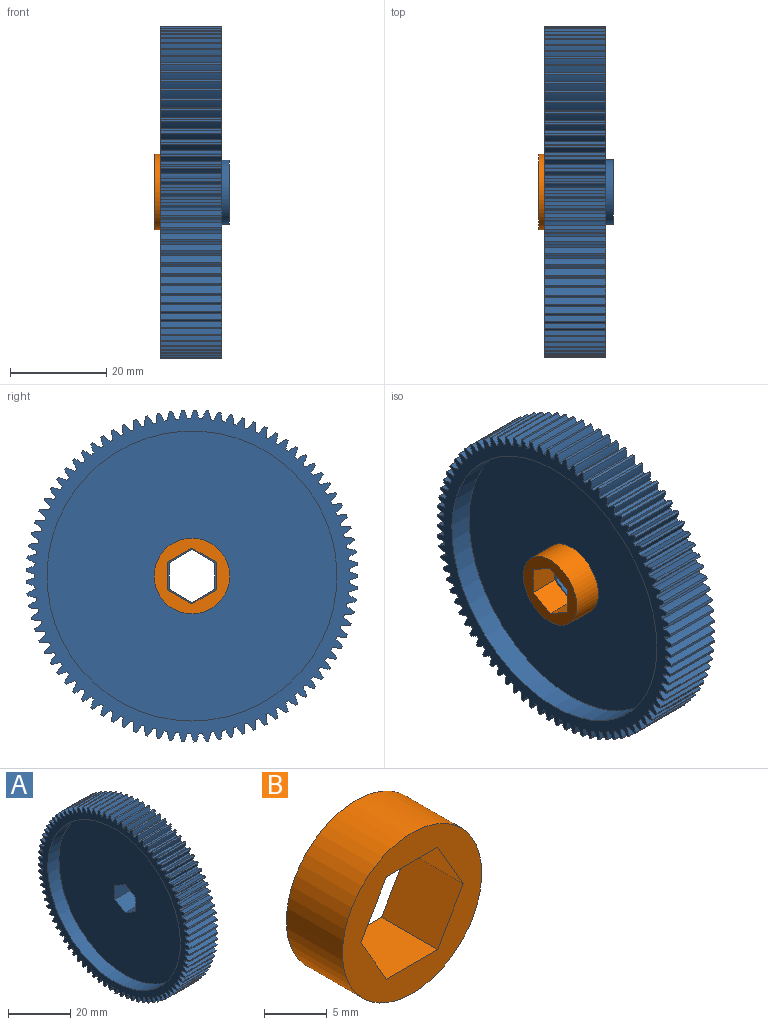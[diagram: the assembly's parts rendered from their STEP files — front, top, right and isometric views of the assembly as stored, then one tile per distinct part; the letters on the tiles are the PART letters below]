
ASSEMBLY  parts=2 mates=1
PART A: 354 faces, bbox 14.3x69x69.1 mm
  f0: cylinder r=30.16mm len=60.33mm, axis (-1,0,0), area 962.7mm2, adj f7,f353
  f1: cylinder r=30.16mm len=60.33mm, axis (1,0,0), area 962.7mm2, adj f8,f352
  f2: cylinder r=6.67mm len=13.34mm, axis (-1,0,0), area 279.3mm2, adj f345,f352
  f3: cylinder r=13.49mm len=12.7mm, axis (-1,0,0), area 24.3mm2, adj f7,f8,f185,f186
  f4: cylinder r=13.49mm len=12.7mm, axis (-1,0,0), area 24.3mm2, adj f7,f8,f187,f188
  f5: cylinder r=13.49mm len=12.7mm, axis (-1,0,0), area 24.3mm2, adj f7,f8,f252,f254
  f6: cylinder r=13.49mm len=12.7mm, axis (-1,0,0), area 24.3mm2, adj f7,f8,f253,f256
  f7: plane 69.05x69.04mm, normal (-1,0,0), area 690.3mm2, adj f0,f3,f4,f5,f6,f9,f10,f11
  f8: plane 69.05x69.04mm, normal (1,0,0), area 690.3mm2, adj f1,f3,f4,f5,f6,f9,f10,f11
  f9: cylinder r=13.49mm len=12.7mm, axis (-1,0,0), area 24.3mm2, adj f7,f8,f175,f176
  f10: cylinder r=13.49mm len=12.7mm, axis (-1,0,0), area 24.3mm2, adj f7,f8,f175,f177
  f11: cylinder r=13.49mm len=12.7mm, axis (-1,0,0), area 24.3mm2, adj f7,f8,f177,f178
  f12: cylinder r=13.49mm len=12.7mm, axis (-1,0,0), area 24.3mm2, adj f7,f8,f178,f179
  f13: cylinder r=13.49mm len=12.7mm, axis (-1,0,0), area 24.3mm2, adj f7,f8,f179,f180
  f14: cylinder r=13.49mm len=12.7mm, axis (-1,0,0), area 24.3mm2, adj f7,f8,f180,f181
  f15: cylinder r=13.49mm len=12.7mm, axis (-1,0,0), area 24.3mm2, adj f7,f8,f181,f182
  f16: cylinder r=13.49mm len=12.7mm, axis (-1,0,0), area 24.3mm2, adj f7,f8,f182,f183
  f17: cylinder r=13.49mm len=12.7mm, axis (-1,0,0), area 24.3mm2, adj f7,f8,f183,f184
  f18: cylinder r=13.49mm len=12.7mm, axis (-1,0,0), area 24.3mm2, adj f7,f8,f184,f185
  f19: cylinder r=13.49mm len=12.7mm, axis (-1,0,0), area 24.3mm2, adj f7,f8,f186,f187
  f20: cylinder r=13.49mm len=12.7mm, axis (-1,0,0), area 24.3mm2, adj f7,f8,f188,f189
  f21: cylinder r=13.49mm len=12.7mm, axis (-1,0,0), area 24.3mm2, adj f7,f8,f189,f190
  f22: cylinder r=13.49mm len=12.7mm, axis (-1,0,0), area 24.3mm2, adj f7,f8,f190,f191
  f23: cylinder r=13.49mm len=12.7mm, axis (-1,0,0), area 24.3mm2, adj f7,f8,f191,f192
  f24: cylinder r=13.49mm len=12.7mm, axis (-1,0,0), area 24.3mm2, adj f7,f8,f192,f193
  f25: cylinder r=13.49mm len=12.7mm, axis (-1,0,0), area 24.3mm2, adj f7,f8,f193,f194
  f26: cylinder r=13.49mm len=12.7mm, axis (-1,0,0), area 24.3mm2, adj f7,f8,f194,f195
  f27: cylinder r=13.49mm len=12.7mm, axis (-1,0,0), area 24.3mm2, adj f7,f8,f195,f196
  f28: cylinder r=13.49mm len=12.7mm, axis (-1,0,0), area 24.3mm2, adj f7,f8,f196,f197
  f29: cylinder r=13.49mm len=12.7mm, axis (-1,0,0), area 24.3mm2, adj f7,f8,f197,f198
  f30: cylinder r=13.49mm len=12.7mm, axis (-1,0,0), area 24.3mm2, adj f7,f8,f198,f199
  f31: cylinder r=13.49mm len=12.7mm, axis (-1,0,0), area 24.3mm2, adj f7,f8,f199,f200
  f32: cylinder r=13.49mm len=12.7mm, axis (-1,0,0), area 24.3mm2, adj f7,f8,f200,f201
  f33: cylinder r=13.49mm len=12.7mm, axis (-1,0,0), area 24.3mm2, adj f7,f8,f201,f202
  f34: cylinder r=13.49mm len=12.7mm, axis (-1,0,0), area 24.3mm2, adj f7,f8,f202,f203
  f35: cylinder r=13.49mm len=12.7mm, axis (-1,0,0), area 24.3mm2, adj f7,f8,f203,f204
  f36: cylinder r=13.49mm len=12.7mm, axis (-1,0,0), area 24.3mm2, adj f7,f8,f204,f205
  f37: cylinder r=13.49mm len=12.7mm, axis (-1,0,0), area 24.3mm2, adj f7,f8,f205,f206
  f38: cylinder r=13.49mm len=12.7mm, axis (-1,0,0), area 24.3mm2, adj f7,f8,f206,f207
  f39: cylinder r=13.49mm len=12.7mm, axis (-1,0,0), area 24.3mm2, adj f7,f8,f207,f208
  f40: cylinder r=13.49mm len=12.7mm, axis (-1,0,0), area 24.3mm2, adj f7,f8,f208,f209
  f41: cylinder r=13.49mm len=12.7mm, axis (-1,0,0), area 24.3mm2, adj f7,f8,f209,f210
  f42: cylinder r=13.49mm len=12.7mm, axis (-1,0,0), area 24.3mm2, adj f7,f8,f210,f211
  f43: cylinder r=13.49mm len=12.7mm, axis (-1,0,0), area 24.3mm2, adj f7,f8,f211,f212
  f44: cylinder r=13.49mm len=12.7mm, axis (-1,0,0), area 24.3mm2, adj f7,f8,f212,f213
  f45: cylinder r=13.49mm len=12.7mm, axis (-1,0,0), area 24.3mm2, adj f7,f8,f213,f214
  f46: cylinder r=13.49mm len=12.7mm, axis (-1,0,0), area 24.3mm2, adj f7,f8,f214,f215
  f47: cylinder r=13.49mm len=12.7mm, axis (-1,0,0), area 24.3mm2, adj f7,f8,f215,f216
  f48: cylinder r=13.49mm len=12.7mm, axis (-1,0,0), area 24.3mm2, adj f7,f8,f216,f217
  f49: cylinder r=13.49mm len=12.7mm, axis (-1,0,0), area 24.3mm2, adj f7,f8,f217,f218
  f50: cylinder r=13.49mm len=12.7mm, axis (-1,0,0), area 24.3mm2, adj f7,f8,f218,f219
  f51: cylinder r=13.49mm len=12.7mm, axis (-1,0,0), area 24.3mm2, adj f7,f8,f219,f220
  f52: cylinder r=13.49mm len=12.7mm, axis (-1,0,0), area 24.3mm2, adj f7,f8,f220,f221
  f53: cylinder r=13.49mm len=12.7mm, axis (-1,0,0), area 24.3mm2, adj f7,f8,f221,f222
  f54: cylinder r=13.49mm len=12.7mm, axis (-1,0,0), area 24.3mm2, adj f7,f8,f222,f223
  f55: cylinder r=13.49mm len=12.7mm, axis (-1,0,0), area 24.3mm2, adj f7,f8,f223,f224
  f56: cylinder r=13.49mm len=12.7mm, axis (-1,0,0), area 24.3mm2, adj f7,f8,f224,f225
  f57: cylinder r=13.49mm len=12.7mm, axis (-1,0,0), area 24.3mm2, adj f7,f8,f225,f226
  f58: cylinder r=13.49mm len=12.7mm, axis (-1,0,0), area 24.3mm2, adj f7,f8,f226,f227
  f59: cylinder r=13.49mm len=12.7mm, axis (-1,0,0), area 24.3mm2, adj f7,f8,f227,f228
  f60: cylinder r=13.49mm len=12.7mm, axis (-1,0,0), area 24.3mm2, adj f7,f8,f228,f229
  f61: cylinder r=13.49mm len=12.7mm, axis (-1,0,0), area 24.3mm2, adj f7,f8,f229,f230
  f62: cylinder r=13.49mm len=12.7mm, axis (-1,0,0), area 24.3mm2, adj f7,f8,f230,f231
  f63: cylinder r=13.49mm len=12.7mm, axis (-1,0,0), area 24.3mm2, adj f7,f8,f231,f232
  f64: cylinder r=13.49mm len=12.7mm, axis (-1,0,0), area 24.3mm2, adj f7,f8,f232,f233
  f65: cylinder r=13.49mm len=12.7mm, axis (-1,0,0), area 24.3mm2, adj f7,f8,f233,f234
  f66: cylinder r=13.49mm len=12.7mm, axis (-1,0,0), area 24.3mm2, adj f7,f8,f234,f235
  f67: cylinder r=13.49mm len=12.7mm, axis (-1,0,0), area 24.3mm2, adj f7,f8,f235,f236
  f68: cylinder r=13.49mm len=12.7mm, axis (-1,0,0), area 24.3mm2, adj f7,f8,f236,f237
  f69: cylinder r=13.49mm len=12.7mm, axis (-1,0,0), area 24.3mm2, adj f7,f8,f237,f238
  f70: cylinder r=13.49mm len=12.7mm, axis (-1,0,0), area 24.3mm2, adj f7,f8,f238,f239
  f71: cylinder r=13.49mm len=12.7mm, axis (-1,0,0), area 24.3mm2, adj f7,f8,f239,f240
  f72: cylinder r=13.49mm len=12.7mm, axis (-1,0,0), area 24.3mm2, adj f7,f8,f240,f241
  f73: cylinder r=13.49mm len=12.7mm, axis (-1,0,0), area 24.3mm2, adj f7,f8,f241,f242
  f74: cylinder r=13.49mm len=12.7mm, axis (-1,0,0), area 24.3mm2, adj f7,f8,f242,f243
  f75: cylinder r=13.49mm len=12.7mm, axis (-1,0,0), area 24.3mm2, adj f7,f8,f243,f244
  f76: cylinder r=13.49mm len=12.7mm, axis (-1,0,0), area 24.3mm2, adj f7,f8,f244,f245
  f77: cylinder r=13.49mm len=12.7mm, axis (-1,0,0), area 24.3mm2, adj f7,f8,f245,f246
  f78: cylinder r=13.49mm len=12.7mm, axis (-1,0,0), area 24.3mm2, adj f7,f8,f246,f247
  f79: cylinder r=13.49mm len=12.7mm, axis (-1,0,0), area 24.3mm2, adj f7,f8,f247,f248
  f80: cylinder r=13.49mm len=12.7mm, axis (-1,0,0), area 24.3mm2, adj f7,f8,f248,f249
  f81: cylinder r=13.49mm len=12.7mm, axis (-1,0,0), area 24.3mm2, adj f7,f8,f249,f250
  f82: cylinder r=13.49mm len=12.7mm, axis (-1,0,0), area 24.3mm2, adj f7,f8,f250,f251
  f83: cylinder r=13.49mm len=12.7mm, axis (-1,0,0), area 24.3mm2, adj f7,f8,f251,f252
  f84: cylinder r=13.49mm len=12.7mm, axis (-1,0,0), area 24.3mm2, adj f7,f8,f253,f254
  f85: cylinder r=13.49mm len=12.7mm, axis (-1,0,0), area 24.3mm2, adj f7,f8,f255,f256
  f86: cylinder r=13.49mm len=12.7mm, axis (-1,0,0), area 24.3mm2, adj f7,f8,f255,f257
  f87: cylinder r=13.49mm len=12.7mm, axis (-1,0,0), area 24.3mm2, adj f7,f8,f257,f258
  f88: cylinder r=13.49mm len=12.7mm, axis (-1,0,0), area 24.3mm2, adj f7,f8,f258,f259
  f89: cylinder r=13.49mm len=12.7mm, axis (-1,0,0), area 24.3mm2, adj f7,f8,f259,f260
  f90: cylinder r=13.49mm len=12.7mm, axis (-1,0,0), area 24.3mm2, adj f7,f8,f260,f261
  f91: cylinder r=13.49mm len=12.7mm, axis (-1,0,0), area 24.3mm2, adj f7,f8,f261,f262
  f92: cylinder r=13.49mm len=12.7mm, axis (-1,0,0), area 24.3mm2, adj f7,f8,f262,f263
  f93: cylinder r=13.49mm len=12.7mm, axis (-1,0,0), area 24.3mm2, adj f7,f8,f263,f264
  f94: cylinder r=13.49mm len=12.7mm, axis (-1,0,0), area 24.3mm2, adj f7,f8,f264,f265
  f95: cylinder r=13.49mm len=12.7mm, axis (-1,0,0), area 24.3mm2, adj f7,f8,f265,f266
  f96: cylinder r=13.49mm len=12.7mm, axis (-1,0,0), area 24.3mm2, adj f7,f8,f266,f267
  f97: cylinder r=13.49mm len=12.7mm, axis (-1,0,0), area 24.3mm2, adj f7,f8,f267,f268
  f98: cylinder r=13.49mm len=12.7mm, axis (-1,0,0), area 24.3mm2, adj f7,f8,f268,f269
  f99: cylinder r=13.49mm len=12.7mm, axis (-1,0,0), area 24.3mm2, adj f7,f8,f269,f270
  f100: cylinder r=13.49mm len=12.7mm, axis (-1,0,0), area 24.3mm2, adj f7,f8,f270,f271
  f101: cylinder r=13.49mm len=12.7mm, axis (-1,0,0), area 24.3mm2, adj f7,f8,f271,f272
  f102: cylinder r=13.49mm len=12.7mm, axis (-1,0,0), area 24.3mm2, adj f7,f8,f272,f273
  f103: cylinder r=13.49mm len=12.7mm, axis (-1,0,0), area 24.3mm2, adj f7,f8,f273,f274
  f104: cylinder r=13.49mm len=12.7mm, axis (-1,0,0), area 24.3mm2, adj f7,f8,f274,f275
  f105: cylinder r=13.49mm len=12.7mm, axis (-1,0,0), area 24.3mm2, adj f7,f8,f275,f276
  f106: cylinder r=13.49mm len=12.7mm, axis (-1,0,0), area 24.3mm2, adj f7,f8,f276,f277
  f107: cylinder r=13.49mm len=12.7mm, axis (-1,0,0), area 24.3mm2, adj f7,f8,f277,f278
  f108: cylinder r=13.49mm len=12.7mm, axis (-1,0,0), area 24.3mm2, adj f7,f8,f278,f279
  f109: cylinder r=13.49mm len=12.7mm, axis (-1,0,0), area 24.3mm2, adj f7,f8,f279,f280
  f110: cylinder r=13.49mm len=12.7mm, axis (-1,0,0), area 24.3mm2, adj f7,f8,f280,f281
  f111: cylinder r=13.49mm len=12.7mm, axis (-1,0,0), area 24.3mm2, adj f7,f8,f281,f282
  f112: cylinder r=13.49mm len=12.7mm, axis (-1,0,0), area 24.3mm2, adj f7,f8,f282,f283
  f113: cylinder r=13.49mm len=12.7mm, axis (-1,0,0), area 24.3mm2, adj f7,f8,f283,f284
  f114: cylinder r=13.49mm len=12.7mm, axis (-1,0,0), area 24.3mm2, adj f7,f8,f284,f285
  f115: cylinder r=13.49mm len=12.7mm, axis (-1,0,0), area 24.3mm2, adj f7,f8,f285,f286
  f116: cylinder r=13.49mm len=12.7mm, axis (-1,0,0), area 24.3mm2, adj f7,f8,f286,f287
  f117: cylinder r=13.49mm len=12.7mm, axis (-1,0,0), area 24.3mm2, adj f7,f8,f287,f288
  f118: cylinder r=13.49mm len=12.7mm, axis (-1,0,0), area 24.3mm2, adj f7,f8,f288,f289
  f119: cylinder r=13.49mm len=12.7mm, axis (-1,0,0), area 24.3mm2, adj f7,f8,f289,f290
  f120: cylinder r=13.49mm len=12.7mm, axis (-1,0,0), area 24.3mm2, adj f7,f8,f290,f291
  f121: cylinder r=13.49mm len=12.7mm, axis (-1,0,0), area 24.3mm2, adj f7,f8,f291,f292
  f122: cylinder r=13.49mm len=12.7mm, axis (-1,0,0), area 24.3mm2, adj f7,f8,f292,f293
  f123: cylinder r=13.49mm len=12.7mm, axis (-1,0,0), area 24.3mm2, adj f7,f8,f293,f294
  f124: cylinder r=13.49mm len=12.7mm, axis (-1,0,0), area 24.3mm2, adj f7,f8,f294,f295
  f125: cylinder r=13.49mm len=12.7mm, axis (-1,0,0), area 24.3mm2, adj f7,f8,f295,f296
  f126: cylinder r=13.49mm len=12.7mm, axis (-1,0,0), area 24.3mm2, adj f7,f8,f296,f297
  f127: cylinder r=13.49mm len=12.7mm, axis (-1,0,0), area 24.3mm2, adj f7,f8,f297,f298
  f128: cylinder r=13.49mm len=12.7mm, axis (-1,0,0), area 24.3mm2, adj f7,f8,f298,f299
  f129: cylinder r=13.49mm len=12.7mm, axis (-1,0,0), area 24.3mm2, adj f7,f8,f299,f300
  f130: cylinder r=13.49mm len=12.7mm, axis (-1,0,0), area 24.3mm2, adj f7,f8,f300,f301
  f131: cylinder r=13.49mm len=12.7mm, axis (-1,0,0), area 24.3mm2, adj f7,f8,f301,f302
  f132: cylinder r=13.49mm len=12.7mm, axis (-1,0,0), area 24.3mm2, adj f7,f8,f302,f303
  f133: cylinder r=13.49mm len=12.7mm, axis (-1,0,0), area 24.3mm2, adj f7,f8,f303,f304
  f134: cylinder r=13.49mm len=12.7mm, axis (-1,0,0), area 24.3mm2, adj f7,f8,f304,f305
  f135: cylinder r=13.49mm len=12.7mm, axis (-1,0,0), area 24.3mm2, adj f7,f8,f305,f306
  f136: cylinder r=13.49mm len=12.7mm, axis (-1,0,0), area 24.3mm2, adj f7,f8,f306,f307
  f137: cylinder r=13.49mm len=12.7mm, axis (-1,0,0), area 24.3mm2, adj f7,f8,f307,f308
  f138: cylinder r=13.49mm len=12.7mm, axis (-1,0,0), area 24.3mm2, adj f7,f8,f308,f309
  f139: cylinder r=13.49mm len=12.7mm, axis (-1,0,0), area 24.3mm2, adj f7,f8,f309,f310
  f140: cylinder r=13.49mm len=12.7mm, axis (-1,0,0), area 24.3mm2, adj f7,f8,f310,f311
  f141: cylinder r=13.49mm len=12.7mm, axis (-1,0,0), area 24.3mm2, adj f7,f8,f311,f312
  f142: cylinder r=13.49mm len=12.7mm, axis (-1,0,0), area 24.3mm2, adj f7,f8,f312,f313
  f143: cylinder r=13.49mm len=12.7mm, axis (-1,0,0), area 24.3mm2, adj f7,f8,f313,f314
  f144: cylinder r=13.49mm len=12.7mm, axis (-1,0,0), area 24.3mm2, adj f7,f8,f314,f315
  f145: cylinder r=13.49mm len=12.7mm, axis (-1,0,0), area 24.3mm2, adj f7,f8,f315,f316
  f146: cylinder r=13.49mm len=12.7mm, axis (-1,0,0), area 24.3mm2, adj f7,f8,f316,f317
  f147: cylinder r=13.49mm len=12.7mm, axis (-1,0,0), area 24.3mm2, adj f7,f8,f317,f318
  f148: cylinder r=13.49mm len=12.7mm, axis (-1,0,0), area 24.3mm2, adj f7,f8,f318,f319
  f149: cylinder r=13.49mm len=12.7mm, axis (-1,0,0), area 24.3mm2, adj f7,f8,f319,f320
  f150: cylinder r=13.49mm len=12.7mm, axis (-1,0,0), area 24.3mm2, adj f7,f8,f320,f321
  f151: cylinder r=13.49mm len=12.7mm, axis (-1,0,0), area 24.3mm2, adj f7,f8,f321,f322
  f152: cylinder r=13.49mm len=12.7mm, axis (-1,0,0), area 24.3mm2, adj f7,f8,f322,f323
  f153: cylinder r=13.49mm len=12.7mm, axis (-1,0,0), area 24.3mm2, adj f7,f8,f323,f324
  f154: cylinder r=13.49mm len=12.7mm, axis (-1,0,0), area 24.3mm2, adj f7,f8,f324,f325
  f155: cylinder r=13.49mm len=12.7mm, axis (-1,0,0), area 24.3mm2, adj f7,f8,f325,f326
  f156: cylinder r=13.49mm len=12.7mm, axis (-1,0,0), area 24.3mm2, adj f7,f8,f326,f327
  f157: cylinder r=13.49mm len=12.7mm, axis (-1,0,0), area 24.3mm2, adj f7,f8,f327,f328
  f158: cylinder r=13.49mm len=12.7mm, axis (-1,0,0), area 24.3mm2, adj f7,f8,f328,f329
  f159: cylinder r=13.49mm len=12.7mm, axis (-1,0,0), area 24.3mm2, adj f7,f8,f329,f330
  f160: cylinder r=13.49mm len=12.7mm, axis (-1,0,0), area 24.3mm2, adj f7,f8,f330,f331
  f161: cylinder r=13.49mm len=12.7mm, axis (-1,0,0), area 24.3mm2, adj f7,f8,f331,f332
  f162: cylinder r=13.49mm len=12.7mm, axis (-1,0,0), area 24.3mm2, adj f7,f8,f332,f333
  f163: cylinder r=13.49mm len=12.7mm, axis (-1,0,0), area 24.3mm2, adj f7,f8,f333,f334
  f164: cylinder r=13.49mm len=12.7mm, axis (-1,0,0), area 24.3mm2, adj f7,f8,f334,f335
  f165: cylinder r=13.49mm len=12.7mm, axis (-1,0,0), area 24.3mm2, adj f7,f8,f335,f336
  f166: cylinder r=13.49mm len=12.7mm, axis (-1,0,0), area 24.3mm2, adj f7,f8,f336,f337
  f167: cylinder r=13.49mm len=12.7mm, axis (-1,0,0), area 24.3mm2, adj f7,f8,f337,f338
  f168: cylinder r=13.49mm len=12.7mm, axis (-1,0,0), area 24.3mm2, adj f7,f8,f338,f339
  f169: cylinder r=13.49mm len=12.7mm, axis (-1,0,0), area 24.3mm2, adj f7,f8,f339,f340
  f170: cylinder r=13.49mm len=12.7mm, axis (-1,0,0), area 24.3mm2, adj f7,f8,f340,f341
  f171: cylinder r=13.49mm len=12.7mm, axis (-1,0,0), area 24.3mm2, adj f7,f8,f341,f342
  f172: cylinder r=13.49mm len=12.7mm, axis (-1,0,0), area 24.3mm2, adj f7,f8,f342,f343
  f173: cylinder r=13.49mm len=12.7mm, axis (-1,0,0), area 24.3mm2, adj f7,f8,f343,f344
  f174: cylinder r=13.49mm len=12.7mm, axis (-1,0,0), area 24.3mm2, adj f7,f8,f176,f344
  f175: cylinder r=32.73mm len=12.7mm, axis (-1,0,0), area 8.3mm2, adj f7,f8,f9,f10
  f176: cylinder r=34.53mm len=12.7mm, axis (-1,0,0), area 6.8mm2, adj f7,f8,f9,f174
  f177: cylinder r=34.53mm len=12.7mm, axis (-1,0,0), area 6.8mm2, adj f7,f8,f10,f11
  f178: cylinder r=32.73mm len=12.7mm, axis (-1,0,0), area 8.3mm2, adj f7,f8,f11,f12
  f179: cylinder r=34.53mm len=12.7mm, axis (-1,0,0), area 6.8mm2, adj f7,f8,f12,f13
  f180: cylinder r=32.73mm len=12.7mm, axis (-1,0,0), area 8.3mm2, adj f7,f8,f13,f14
  f181: cylinder r=34.53mm len=12.7mm, axis (-1,0,0), area 6.8mm2, adj f7,f8,f14,f15
  f182: cylinder r=32.73mm len=12.7mm, axis (-1,0,0), area 8.3mm2, adj f7,f8,f15,f16
  f183: cylinder r=34.53mm len=12.7mm, axis (-1,0,0), area 6.8mm2, adj f7,f8,f16,f17
  f184: cylinder r=32.73mm len=12.7mm, axis (-1,0,0), area 8.3mm2, adj f7,f8,f17,f18
  f185: cylinder r=34.53mm len=12.7mm, axis (-1,0,0), area 6.8mm2, adj f3,f7,f8,f18
  f186: cylinder r=32.73mm len=12.7mm, axis (-1,0,0), area 8.3mm2, adj f3,f7,f8,f19
  f187: cylinder r=34.53mm len=12.7mm, axis (-1,0,0), area 6.8mm2, adj f4,f7,f8,f19
  f188: cylinder r=32.73mm len=12.7mm, axis (-1,0,0), area 8.3mm2, adj f4,f7,f8,f20
  f189: cylinder r=34.53mm len=12.7mm, axis (-1,0,0), area 6.8mm2, adj f7,f8,f20,f21
  f190: cylinder r=32.73mm len=12.7mm, axis (-1,0,0), area 8.3mm2, adj f7,f8,f21,f22
  f191: cylinder r=34.53mm len=12.7mm, axis (-1,0,0), area 6.8mm2, adj f7,f8,f22,f23
  f192: cylinder r=32.73mm len=12.7mm, axis (-1,0,0), area 8.3mm2, adj f7,f8,f23,f24
  f193: cylinder r=34.53mm len=12.7mm, axis (-1,0,0), area 6.8mm2, adj f7,f8,f24,f25
  f194: cylinder r=32.73mm len=12.7mm, axis (-1,0,0), area 8.3mm2, adj f7,f8,f25,f26
  f195: cylinder r=34.53mm len=12.7mm, axis (-1,0,0), area 6.8mm2, adj f7,f8,f26,f27
  f196: cylinder r=32.73mm len=12.7mm, axis (-1,0,0), area 8.3mm2, adj f7,f8,f27,f28
  f197: cylinder r=34.53mm len=12.7mm, axis (-1,0,0), area 6.8mm2, adj f7,f8,f28,f29
  f198: cylinder r=32.73mm len=12.7mm, axis (-1,0,0), area 8.3mm2, adj f7,f8,f29,f30
  f199: cylinder r=34.53mm len=12.7mm, axis (-1,0,0), area 6.8mm2, adj f7,f8,f30,f31
  f200: cylinder r=32.73mm len=12.7mm, axis (-1,0,0), area 8.3mm2, adj f7,f8,f31,f32
  f201: cylinder r=34.53mm len=12.7mm, axis (-1,0,0), area 6.8mm2, adj f7,f8,f32,f33
  f202: cylinder r=32.73mm len=12.7mm, axis (-1,0,0), area 8.3mm2, adj f7,f8,f33,f34
  f203: cylinder r=34.53mm len=12.7mm, axis (-1,0,0), area 6.8mm2, adj f7,f8,f34,f35
  f204: cylinder r=32.73mm len=12.7mm, axis (-1,0,0), area 8.3mm2, adj f7,f8,f35,f36
  f205: cylinder r=34.53mm len=12.7mm, axis (-1,0,0), area 6.8mm2, adj f7,f8,f36,f37
  f206: cylinder r=32.73mm len=12.7mm, axis (-1,0,0), area 8.3mm2, adj f7,f8,f37,f38
  f207: cylinder r=34.53mm len=12.7mm, axis (-1,0,0), area 6.8mm2, adj f7,f8,f38,f39
  f208: cylinder r=32.73mm len=12.7mm, axis (-1,0,0), area 8.3mm2, adj f7,f8,f39,f40
  f209: cylinder r=34.53mm len=12.7mm, axis (-1,0,0), area 6.8mm2, adj f7,f8,f40,f41
  f210: cylinder r=32.73mm len=12.7mm, axis (-1,0,0), area 8.3mm2, adj f7,f8,f41,f42
  f211: cylinder r=34.53mm len=12.7mm, axis (-1,0,0), area 6.8mm2, adj f7,f8,f42,f43
  f212: cylinder r=32.73mm len=12.7mm, axis (-1,0,0), area 8.3mm2, adj f7,f8,f43,f44
  f213: cylinder r=34.53mm len=12.7mm, axis (-1,0,0), area 6.8mm2, adj f7,f8,f44,f45
  f214: cylinder r=32.73mm len=12.7mm, axis (-1,0,0), area 8.3mm2, adj f7,f8,f45,f46
  f215: cylinder r=34.53mm len=12.7mm, axis (-1,0,0), area 6.8mm2, adj f7,f8,f46,f47
  f216: cylinder r=32.73mm len=12.7mm, axis (-1,0,0), area 8.3mm2, adj f7,f8,f47,f48
  f217: cylinder r=34.53mm len=12.7mm, axis (-1,0,0), area 6.8mm2, adj f7,f8,f48,f49
  f218: cylinder r=32.73mm len=12.7mm, axis (-1,0,0), area 8.3mm2, adj f7,f8,f49,f50
  f219: cylinder r=34.53mm len=12.7mm, axis (-1,0,0), area 6.8mm2, adj f7,f8,f50,f51
  f220: cylinder r=32.73mm len=12.7mm, axis (-1,0,0), area 8.3mm2, adj f7,f8,f51,f52
  f221: cylinder r=34.53mm len=12.7mm, axis (-1,0,0), area 6.8mm2, adj f7,f8,f52,f53
  f222: cylinder r=32.73mm len=12.7mm, axis (-1,0,0), area 8.3mm2, adj f7,f8,f53,f54
  f223: cylinder r=34.53mm len=12.7mm, axis (-1,0,0), area 6.8mm2, adj f7,f8,f54,f55
  f224: cylinder r=32.73mm len=12.7mm, axis (-1,0,0), area 8.3mm2, adj f7,f8,f55,f56
  f225: cylinder r=34.53mm len=12.7mm, axis (-1,0,0), area 6.8mm2, adj f7,f8,f56,f57
  f226: cylinder r=32.73mm len=12.7mm, axis (-1,0,0), area 8.3mm2, adj f7,f8,f57,f58
  f227: cylinder r=34.53mm len=12.7mm, axis (-1,0,0), area 6.8mm2, adj f7,f8,f58,f59
  f228: cylinder r=32.73mm len=12.7mm, axis (-1,0,0), area 8.3mm2, adj f7,f8,f59,f60
  f229: cylinder r=34.53mm len=12.7mm, axis (-1,0,0), area 6.8mm2, adj f7,f8,f60,f61
  f230: cylinder r=32.73mm len=12.7mm, axis (-1,0,0), area 8.3mm2, adj f7,f8,f61,f62
  f231: cylinder r=34.53mm len=12.7mm, axis (-1,0,0), area 6.8mm2, adj f7,f8,f62,f63
  f232: cylinder r=32.73mm len=12.7mm, axis (-1,0,0), area 8.3mm2, adj f7,f8,f63,f64
  f233: cylinder r=34.53mm len=12.7mm, axis (-1,0,0), area 6.8mm2, adj f7,f8,f64,f65
  f234: cylinder r=32.73mm len=12.7mm, axis (-1,0,0), area 8.3mm2, adj f7,f8,f65,f66
  f235: cylinder r=34.53mm len=12.7mm, axis (-1,0,0), area 6.8mm2, adj f7,f8,f66,f67
  f236: cylinder r=32.73mm len=12.7mm, axis (-1,0,0), area 8.3mm2, adj f7,f8,f67,f68
  f237: cylinder r=34.53mm len=12.7mm, axis (-1,0,0), area 6.8mm2, adj f7,f8,f68,f69
  f238: cylinder r=32.73mm len=12.7mm, axis (-1,0,0), area 8.3mm2, adj f7,f8,f69,f70
  f239: cylinder r=34.53mm len=12.7mm, axis (-1,0,0), area 6.8mm2, adj f7,f8,f70,f71
  f240: cylinder r=32.73mm len=12.7mm, axis (-1,0,0), area 8.3mm2, adj f7,f8,f71,f72
  f241: cylinder r=34.53mm len=12.7mm, axis (-1,0,0), area 6.8mm2, adj f7,f8,f72,f73
  f242: cylinder r=32.73mm len=12.7mm, axis (-1,0,0), area 8.3mm2, adj f7,f8,f73,f74
  f243: cylinder r=34.53mm len=12.7mm, axis (-1,0,0), area 6.8mm2, adj f7,f8,f74,f75
  f244: cylinder r=32.73mm len=12.7mm, axis (-1,0,0), area 8.3mm2, adj f7,f8,f75,f76
  f245: cylinder r=34.53mm len=12.7mm, axis (-1,0,0), area 6.8mm2, adj f7,f8,f76,f77
  f246: cylinder r=32.73mm len=12.7mm, axis (-1,0,0), area 8.3mm2, adj f7,f8,f77,f78
  f247: cylinder r=34.53mm len=12.7mm, axis (-1,0,0), area 6.8mm2, adj f7,f8,f78,f79
  f248: cylinder r=32.73mm len=12.7mm, axis (-1,0,0), area 8.3mm2, adj f7,f8,f79,f80
  f249: cylinder r=34.53mm len=12.7mm, axis (-1,0,0), area 6.8mm2, adj f7,f8,f80,f81
  f250: cylinder r=32.73mm len=12.7mm, axis (-1,0,0), area 8.3mm2, adj f7,f8,f81,f82
  f251: cylinder r=34.53mm len=12.7mm, axis (-1,0,0), area 6.8mm2, adj f7,f8,f82,f83
  f252: cylinder r=32.73mm len=12.7mm, axis (-1,0,0), area 8.3mm2, adj f5,f7,f8,f83
  f253: cylinder r=32.73mm len=12.7mm, axis (-1,0,0), area 8.3mm2, adj f6,f7,f8,f84
  f254: cylinder r=34.53mm len=12.7mm, axis (-1,0,0), area 6.8mm2, adj f5,f7,f8,f84
  f255: cylinder r=32.73mm len=12.7mm, axis (-1,0,0), area 8.3mm2, adj f7,f8,f85,f86
  f256: cylinder r=34.53mm len=12.7mm, axis (-1,0,0), area 6.8mm2, adj f6,f7,f8,f85
  f257: cylinder r=34.53mm len=12.7mm, axis (-1,0,0), area 6.8mm2, adj f7,f8,f86,f87
  f258: cylinder r=32.73mm len=12.7mm, axis (-1,0,0), area 8.3mm2, adj f7,f8,f87,f88
  f259: cylinder r=34.53mm len=12.7mm, axis (-1,0,0), area 6.8mm2, adj f7,f8,f88,f89
  f260: cylinder r=32.73mm len=12.7mm, axis (-1,0,0), area 8.3mm2, adj f7,f8,f89,f90
  f261: cylinder r=34.53mm len=12.7mm, axis (-1,0,0), area 6.8mm2, adj f7,f8,f90,f91
  f262: cylinder r=32.73mm len=12.7mm, axis (-1,0,0), area 8.3mm2, adj f7,f8,f91,f92
  f263: cylinder r=34.53mm len=12.7mm, axis (-1,0,0), area 6.8mm2, adj f7,f8,f92,f93
  f264: cylinder r=32.73mm len=12.7mm, axis (-1,0,0), area 8.3mm2, adj f7,f8,f93,f94
  f265: cylinder r=34.53mm len=12.7mm, axis (-1,0,0), area 6.8mm2, adj f7,f8,f94,f95
  f266: cylinder r=32.73mm len=12.7mm, axis (-1,0,0), area 8.3mm2, adj f7,f8,f95,f96
  f267: cylinder r=34.53mm len=12.7mm, axis (-1,0,0), area 6.8mm2, adj f7,f8,f96,f97
  f268: cylinder r=32.73mm len=12.7mm, axis (-1,0,0), area 8.3mm2, adj f7,f8,f97,f98
  f269: cylinder r=34.53mm len=12.7mm, axis (-1,0,0), area 6.8mm2, adj f7,f8,f98,f99
  f270: cylinder r=32.73mm len=12.7mm, axis (-1,0,0), area 8.3mm2, adj f7,f8,f99,f100
  f271: cylinder r=34.53mm len=12.7mm, axis (-1,0,0), area 6.8mm2, adj f7,f8,f100,f101
  f272: cylinder r=32.73mm len=12.7mm, axis (-1,0,0), area 8.3mm2, adj f7,f8,f101,f102
  f273: cylinder r=34.53mm len=12.7mm, axis (-1,0,0), area 6.8mm2, adj f7,f8,f102,f103
  f274: cylinder r=32.73mm len=12.7mm, axis (-1,0,0), area 8.3mm2, adj f7,f8,f103,f104
  f275: cylinder r=34.53mm len=12.7mm, axis (-1,0,0), area 6.8mm2, adj f7,f8,f104,f105
  f276: cylinder r=32.73mm len=12.7mm, axis (-1,0,0), area 8.3mm2, adj f7,f8,f105,f106
  f277: cylinder r=34.53mm len=12.7mm, axis (-1,0,0), area 6.8mm2, adj f7,f8,f106,f107
  f278: cylinder r=32.73mm len=12.7mm, axis (-1,0,0), area 8.3mm2, adj f7,f8,f107,f108
  f279: cylinder r=34.53mm len=12.7mm, axis (-1,0,0), area 6.8mm2, adj f7,f8,f108,f109
  f280: cylinder r=32.73mm len=12.7mm, axis (-1,0,0), area 8.3mm2, adj f7,f8,f109,f110
  f281: cylinder r=34.53mm len=12.7mm, axis (-1,0,0), area 6.8mm2, adj f7,f8,f110,f111
  f282: cylinder r=32.73mm len=12.7mm, axis (-1,0,0), area 8.3mm2, adj f7,f8,f111,f112
  f283: cylinder r=34.53mm len=12.7mm, axis (-1,0,0), area 6.8mm2, adj f7,f8,f112,f113
  f284: cylinder r=32.73mm len=12.7mm, axis (-1,0,0), area 8.3mm2, adj f7,f8,f113,f114
  f285: cylinder r=34.53mm len=12.7mm, axis (-1,0,0), area 6.8mm2, adj f7,f8,f114,f115
  f286: cylinder r=32.73mm len=12.7mm, axis (-1,0,0), area 8.3mm2, adj f7,f8,f115,f116
  f287: cylinder r=34.53mm len=12.7mm, axis (-1,0,0), area 6.8mm2, adj f7,f8,f116,f117
  f288: cylinder r=32.73mm len=12.7mm, axis (-1,0,0), area 8.3mm2, adj f7,f8,f117,f118
  f289: cylinder r=34.53mm len=12.7mm, axis (-1,0,0), area 6.8mm2, adj f7,f8,f118,f119
  f290: cylinder r=32.73mm len=12.7mm, axis (-1,0,0), area 8.3mm2, adj f7,f8,f119,f120
  f291: cylinder r=34.53mm len=12.7mm, axis (-1,0,0), area 6.8mm2, adj f7,f8,f120,f121
  f292: cylinder r=32.73mm len=12.7mm, axis (-1,0,0), area 8.3mm2, adj f7,f8,f121,f122
  f293: cylinder r=34.53mm len=12.7mm, axis (-1,0,0), area 6.8mm2, adj f7,f8,f122,f123
  f294: cylinder r=32.73mm len=12.7mm, axis (-1,0,0), area 8.3mm2, adj f7,f8,f123,f124
  f295: cylinder r=34.53mm len=12.7mm, axis (-1,0,0), area 6.8mm2, adj f7,f8,f124,f125
  f296: cylinder r=32.73mm len=12.7mm, axis (-1,0,0), area 8.3mm2, adj f7,f8,f125,f126
  f297: cylinder r=34.53mm len=12.7mm, axis (-1,0,0), area 6.8mm2, adj f7,f8,f126,f127
  f298: cylinder r=32.73mm len=12.7mm, axis (-1,0,0), area 8.3mm2, adj f7,f8,f127,f128
  f299: cylinder r=34.53mm len=12.7mm, axis (-1,0,0), area 6.8mm2, adj f7,f8,f128,f129
  f300: cylinder r=32.73mm len=12.7mm, axis (-1,0,0), area 8.3mm2, adj f7,f8,f129,f130
  f301: cylinder r=34.53mm len=12.7mm, axis (-1,0,0), area 6.8mm2, adj f7,f8,f130,f131
  f302: cylinder r=32.73mm len=12.7mm, axis (-1,0,0), area 8.3mm2, adj f7,f8,f131,f132
  f303: cylinder r=34.53mm len=12.7mm, axis (-1,0,0), area 6.8mm2, adj f7,f8,f132,f133
  f304: cylinder r=32.73mm len=12.7mm, axis (-1,0,0), area 8.3mm2, adj f7,f8,f133,f134
  f305: cylinder r=34.53mm len=12.7mm, axis (-1,0,0), area 6.8mm2, adj f7,f8,f134,f135
  f306: cylinder r=32.73mm len=12.7mm, axis (-1,0,0), area 8.3mm2, adj f7,f8,f135,f136
  f307: cylinder r=34.53mm len=12.7mm, axis (-1,0,0), area 6.8mm2, adj f7,f8,f136,f137
  f308: cylinder r=32.73mm len=12.7mm, axis (-1,0,0), area 8.3mm2, adj f7,f8,f137,f138
  f309: cylinder r=34.53mm len=12.7mm, axis (-1,0,0), area 6.8mm2, adj f7,f8,f138,f139
  f310: cylinder r=32.73mm len=12.7mm, axis (-1,0,0), area 8.3mm2, adj f7,f8,f139,f140
  f311: cylinder r=34.53mm len=12.7mm, axis (-1,0,0), area 6.8mm2, adj f7,f8,f140,f141
  f312: cylinder r=32.73mm len=12.7mm, axis (-1,0,0), area 8.3mm2, adj f7,f8,f141,f142
  f313: cylinder r=34.53mm len=12.7mm, axis (-1,0,0), area 6.8mm2, adj f7,f8,f142,f143
  f314: cylinder r=32.73mm len=12.7mm, axis (-1,0,0), area 8.3mm2, adj f7,f8,f143,f144
  f315: cylinder r=34.53mm len=12.7mm, axis (-1,0,0), area 6.8mm2, adj f7,f8,f144,f145
  f316: cylinder r=32.73mm len=12.7mm, axis (-1,0,0), area 8.3mm2, adj f7,f8,f145,f146
  f317: cylinder r=34.53mm len=12.7mm, axis (-1,0,0), area 6.8mm2, adj f7,f8,f146,f147
  f318: cylinder r=32.73mm len=12.7mm, axis (-1,0,0), area 8.3mm2, adj f7,f8,f147,f148
  f319: cylinder r=34.53mm len=12.7mm, axis (-1,0,0), area 6.8mm2, adj f7,f8,f148,f149
  f320: cylinder r=32.73mm len=12.7mm, axis (-1,0,0), area 8.3mm2, adj f7,f8,f149,f150
  f321: cylinder r=34.53mm len=12.7mm, axis (-1,0,0), area 6.8mm2, adj f7,f8,f150,f151
  f322: cylinder r=32.73mm len=12.7mm, axis (-1,0,0), area 8.3mm2, adj f7,f8,f151,f152
  f323: cylinder r=34.53mm len=12.7mm, axis (-1,0,0), area 6.8mm2, adj f7,f8,f152,f153
  f324: cylinder r=32.73mm len=12.7mm, axis (-1,0,0), area 8.3mm2, adj f7,f8,f153,f154
  f325: cylinder r=34.53mm len=12.7mm, axis (-1,0,0), area 6.8mm2, adj f7,f8,f154,f155
  f326: cylinder r=32.73mm len=12.7mm, axis (-1,0,0), area 8.3mm2, adj f7,f8,f155,f156
  f327: cylinder r=34.53mm len=12.7mm, axis (-1,0,0), area 6.8mm2, adj f7,f8,f156,f157
  f328: cylinder r=32.73mm len=12.7mm, axis (-1,0,0), area 8.3mm2, adj f7,f8,f157,f158
  f329: cylinder r=34.53mm len=12.7mm, axis (-1,0,0), area 6.8mm2, adj f7,f8,f158,f159
  f330: cylinder r=32.73mm len=12.7mm, axis (-1,0,0), area 8.3mm2, adj f7,f8,f159,f160
  f331: cylinder r=34.53mm len=12.7mm, axis (-1,0,0), area 6.8mm2, adj f7,f8,f160,f161
  f332: cylinder r=32.73mm len=12.7mm, axis (-1,0,0), area 8.3mm2, adj f7,f8,f161,f162
  f333: cylinder r=34.53mm len=12.7mm, axis (-1,0,0), area 6.8mm2, adj f7,f8,f162,f163
  f334: cylinder r=32.73mm len=12.7mm, axis (-1,0,0), area 8.3mm2, adj f7,f8,f163,f164
  f335: cylinder r=34.53mm len=12.7mm, axis (-1,0,0), area 6.8mm2, adj f7,f8,f164,f165
  f336: cylinder r=32.73mm len=12.7mm, axis (-1,0,0), area 8.3mm2, adj f7,f8,f165,f166
  f337: cylinder r=34.53mm len=12.7mm, axis (-1,0,0), area 6.8mm2, adj f7,f8,f166,f167
  f338: cylinder r=32.73mm len=12.7mm, axis (-1,0,0), area 8.3mm2, adj f7,f8,f167,f168
  f339: cylinder r=34.53mm len=12.7mm, axis (-1,0,0), area 6.8mm2, adj f7,f8,f168,f169
  f340: cylinder r=32.73mm len=12.7mm, axis (-1,0,0), area 8.3mm2, adj f7,f8,f169,f170
  f341: cylinder r=34.53mm len=12.7mm, axis (-1,0,0), area 6.8mm2, adj f7,f8,f170,f171
  f342: cylinder r=32.73mm len=12.7mm, axis (-1,0,0), area 8.3mm2, adj f7,f8,f171,f172
  f343: cylinder r=34.53mm len=12.7mm, axis (-1,0,0), area 6.8mm2, adj f7,f8,f172,f173
  f344: cylinder r=32.73mm len=12.7mm, axis (-1,0,0), area 8.3mm2, adj f7,f8,f173,f174
  f345: plane 13.34x13.34mm, normal (1,0,0), area 60.7mm2, adj f2,f346,f347,f348,f349,f350,f351
  f346: plane 9.21x4.78mm, normal (0,0.5,0.87), area 50.8mm2, adj f345,f347,f351,f353
  f347: plane 9.21x5.51mm, normal (0,1,0), area 50.8mm2, adj f345,f346,f348,f353
  f348: plane 9.21x4.78mm, normal (0,0.5,-0.87), area 50.8mm2, adj f345,f347,f349,f353
  f349: plane 9.21x4.78mm, normal (0,-0.5,-0.87), area 50.8mm2, adj f345,f348,f350,f353
  f350: plane 9.21x5.51mm, normal (0,-1,0), area 50.8mm2, adj f345,f349,f351,f353
  f351: plane 9.21x4.78mm, normal (0,-0.5,0.87), area 50.8mm2, adj f345,f346,f350,f353
  f352: plane 60.33x60.33mm, normal (1,0,0), area 2718.5mm2, adj f1,f2
  f353: plane 60.33x60.33mm, normal (-1,0,0), area 2779.2mm2, adj f0,f346,f347,f348,f349,f350,f351
PART B: 9 faces, bbox 15.7x6.4x15.7 mm
  f0: plane 6.35x5.79mm, normal (0,0,-1), area 36.8mm2, adj f1,f6,f7,f8
  f1: plane 6.35x5.02mm, normal (-0.87,0,-0.5), area 36.8mm2, adj f0,f2,f7,f8
  f2: plane 6.35x5.02mm, normal (-0.87,0,0.5), area 36.8mm2, adj f1,f3,f7,f8
  f3: plane 6.35x5.79mm, normal (0,0,1), area 36.8mm2, adj f2,f4,f7,f8
  f4: plane 6.35x5.02mm, normal (0.87,0,0.5), area 36.8mm2, adj f3,f6,f7,f8
  f5: cylinder r=7.87mm len=15.75mm, axis (0,1,0), area 314.2mm2, adj f7,f8
  f6: plane 6.35x5.02mm, normal (0.87,0,-0.5), area 36.8mm2, adj f0,f4,f7,f8
  f7: plane 15.75x15.75mm, normal (0,-1,0), area 107.6mm2, adj f0,f1,f2,f3,f4,f5,f6
  f8: plane 15.75x15.75mm, normal (0,1,0), area 107.6mm2, adj f0,f1,f2,f3,f4,f5,f6
PLACE A t=(-20.36,-9.93,-3.47)mm
PLACE B rot(axis=(-0.58,-0.58,-0.58),120deg) t=(-15.28,-9.93,-3.47)mm
MATE fastened B.f5 <-> A.f0  axis (1,0,0) through (-15.28,-9.93,-3.47)mm
